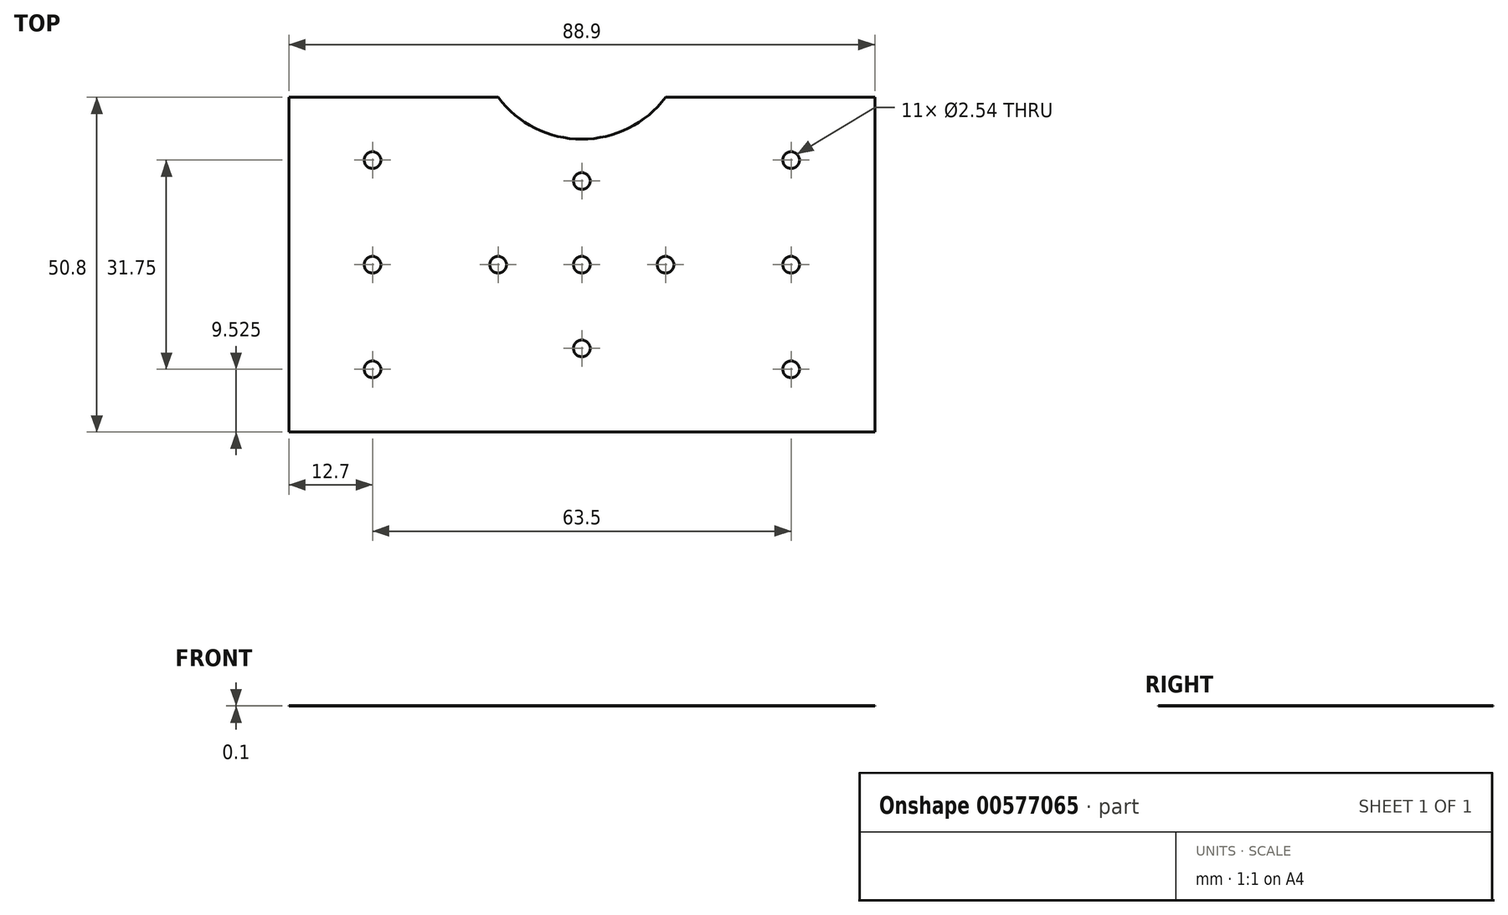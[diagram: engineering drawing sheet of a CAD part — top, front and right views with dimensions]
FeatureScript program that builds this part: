
annotation { "Feature Type Name" : "Feature", "Feature Type Description" : "" }
export const myFeature = defineFeature(function(context is Context, id is Id, definition is map)
    precondition{}
    {
        {
            var Q0;
            Q0=qCreatedBy(makeId("Top.planeOp"),FACE);
            var sketch = newSketch(context, id + "F0", { "sketchPlane" : qUnion([Q0])});
            skLineSegment(sketch, "E0.bottom", {"start": v(0, 0) * mm, "end": v(88.9, 0) * mm});
            skLineSegment(sketch, "E0.top", {"start": v(0, 50.8) * mm, "end": v(88.9, 50.8) * mm});
            skLineSegment(sketch, "E0.left", {"start": v(0, 0) * mm, "end": v(0, 50.8) * mm});
            skLineSegment(sketch, "E0.right", {"start": v(88.9, 0) * mm, "end": v(88.9, 50.8) * mm});
            skCircle(sketch, "E1", {"center": v(44.45, 25.4) * mm, "radius": 1.27 * mm});
            skPoint(sketch, "E1.centerSnap0", {"position": v(88.9, 25.4) * mm});
            skCircle(sketch, "E2.1.0.0", {"center": v(57.15, 25.4) * mm, "radius": 1.27 * mm});
            skLineSegment(sketch, "E2.direction1", {"start": v(44.45, 25.4) * mm, "end": v(57.15, 25.4) * mm, "construction": true});
            skCircle(sketch, "E3.1.0", {"center": v(44.45, 38.1) * mm, "radius": 1.27 * mm});
            skCircle(sketch, "E3.2.0", {"center": v(31.75, 25.4) * mm, "radius": 1.27 * mm});
            skCircle(sketch, "E3.3.0", {"center": v(44.45, 12.7) * mm, "radius": 1.27 * mm});
            skLineSegment(sketch, "E4", {"start": v(44.45, 0) * mm, "end": v(44.45, 11.43) * mm});
            skCircle(sketch, "E5", {"center": v(12.7, 25.4) * mm, "radius": 1.27 * mm});
            skCircle(sketch, "E6", {"center": v(12.7, 41.27) * mm, "radius": 1.27 * mm});
            skLineSegment(sketch, "E7", {"start": v(0, 25.4) * mm, "end": v(11.43, 25.4) * mm});
            skCircle(sketch, "E8.MirrorC", {"center": v(12.7, 9.53) * mm, "radius": 1.27 * mm});
            skCircle(sketch, "E9.MirrorC", {"center": v(76.2, 9.53) * mm, "radius": 1.27 * mm});
            skCircle(sketch, "E10.MirrorC", {"center": v(76.2, 25.4) * mm, "radius": 1.27 * mm});
            skCircle(sketch, "E11.MirrorC", {"center": v(76.2, 41.27) * mm, "radius": 1.27 * mm});
            skPoint(sketch, "E12", {"position": v(44.45, 44.45) * mm});
            skPoint(sketch, "E12.positionSnap0", {"position": v(44.45, 50.8) * mm});
            skPoint(sketch, "E13", {"position": v(57.15, 50.8) * mm});
            skPoint(sketch, "E14", {"position": v(31.75, 50.8) * mm});
            skArc(sketch, "E15", {"start": v(31.75, 50.8) * mm, "mid": v(44.45, 44.45) * mm, "end": v(57.15, 50.8) * mm});
            skSolve(sketch);
        }
        {
            var Q0;
            {var subQ0=sQuery(id+"F0.wireOp",EDGE,"E0.right");Q0=makeQuery(id+"F0.imprint","IMPRINT",FACE,{"disambiguationData":[TD([[makeQuery(id+"F0.imprint","IMPRINT",EDGE,{"derivedFrom":subQ0}),1.0]])]});}
            extrude(context, id + "F1", {"entities" : qUnion([Q0]), "depth" : .1 * mm, "offsetDistance" : 25.4 * mm});
        }
    });
